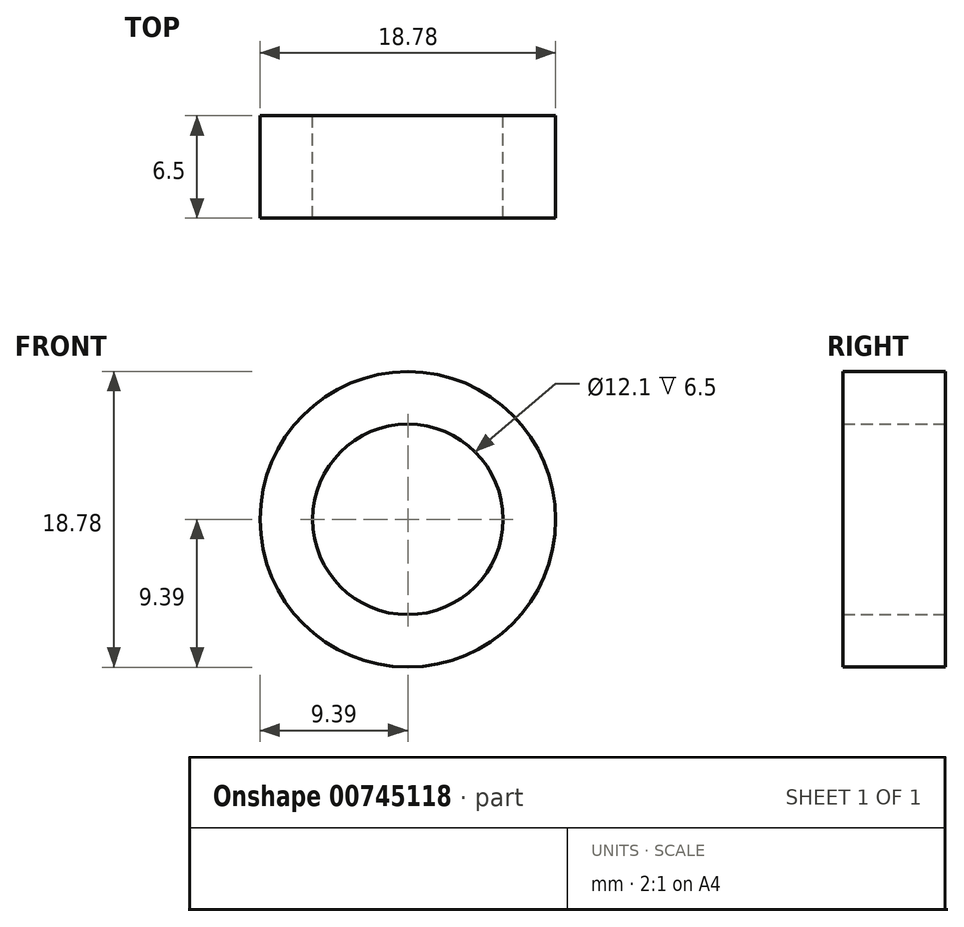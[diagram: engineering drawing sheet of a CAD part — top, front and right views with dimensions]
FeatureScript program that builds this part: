
annotation { "Feature Type Name" : "Feature", "Feature Type Description" : "" }
export const myFeature = defineFeature(function(context is Context, id is Id, definition is map)
    precondition{}
    {
        {
            var Q0;
            Q0=qCreatedBy(makeId("Front.planeOp"),FACE);
            var sketch = newSketch(context, id + "F0", { "sketchPlane" : qUnion([Q0])});
            skCircle(sketch, "E0", {"center": v(0, 0) * mm, "radius": 9.38 * mm});
            skCircle(sketch, "E1", {"center": v(0, 0) * mm, "radius": 6.05 * mm});
            skSolve(sketch);
        }
        {
            var Q0;
            Q0 = qSketchRegion(id + "F0", true);
            extrude(context, id + "F1", {"entities" : qUnion([Q0]), "endBound" : BoundingType.SYMMETRIC, "depth" : 6.5 * mm, "offsetDistance" : 25 * mm});
        }
    });
